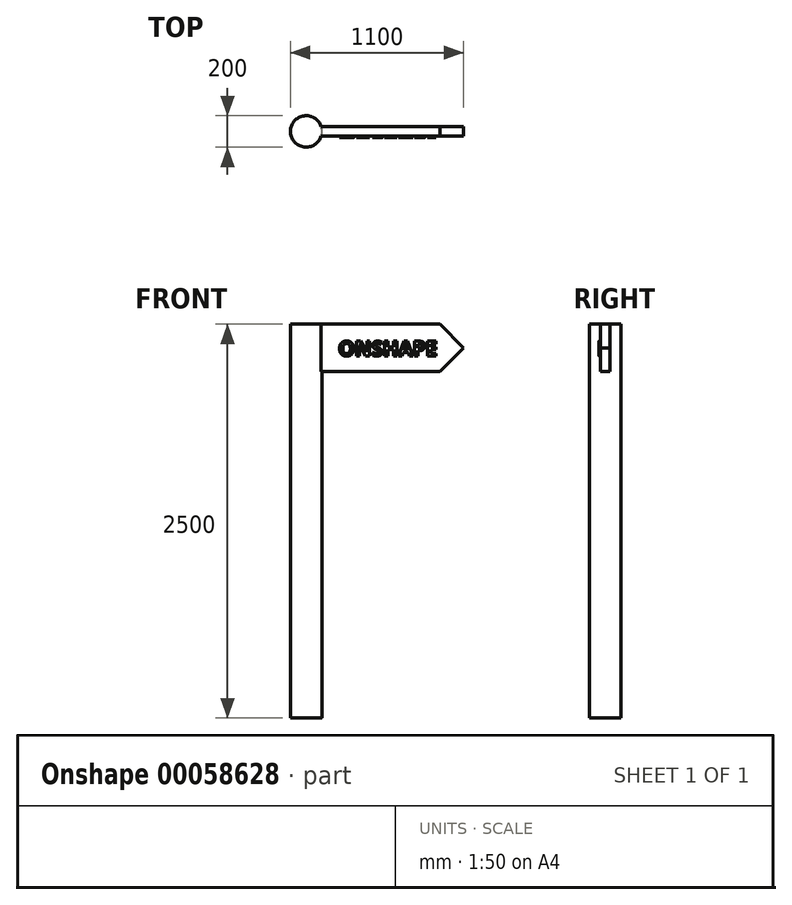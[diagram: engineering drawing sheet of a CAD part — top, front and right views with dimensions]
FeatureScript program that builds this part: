
annotation { "Feature Type Name" : "Feature", "Feature Type Description" : "" }
export const myFeature = defineFeature(function(context is Context, id is Id, definition is map)
    precondition{}
    {
        {
            var Q0;
            Q0=qCreatedBy(makeId("Top.planeOp"),FACE);
            var sketch = newSketch(context, id + "F0", { "sketchPlane" : qUnion([Q0])});
            skCircle(sketch, "E0", {"center": v(0, 0) * mm, "radius": 100 * mm});
            skSolve(sketch);
        }
        {
            var Q0;
            Q0 = qSketchRegion(id + "F0", true);
            extrude(context, id + "F1", {"entities" : qUnion([Q0]), "depth" : 2500 * mm});
        }
        {
            var Q0;
            Q0=qCreatedBy(makeId("Front.planeOp"),FACE);
            var sketch = newSketch(context, id + "F2", { "sketchPlane" : qUnion([Q0])});
            skLineSegment(sketch, "E1.bottom", {"start": v(0, 2500) * mm, "end": v(1000, 2500) * mm});
            skLineSegment(sketch, "E1.top", {"start": v(0, 2200) * mm, "end": v(1000, 2200) * mm});
            skLineSegment(sketch, "E1.left", {"start": v(0, 2500) * mm, "end": v(0, 2200) * mm});
            skLineSegment(sketch, "E1.right", {"start": v(1000, 2500) * mm, "end": v(1000, 2200) * mm});
            skLineSegment(sketch, "E2", {"start": v(1000, 2350) * mm, "end": v(850, 2500) * mm});
            skLineSegment(sketch, "E3", {"start": v(1000, 2350) * mm, "end": v(850, 2200) * mm});
            skSolve(sketch);
        }
        {
            var Q0;
            {var subQ1=sQuery(id+"F2.wireOp",EDGE,"E1.left");Q0=makeQuery(id+"F2.imprint","IMPRINT",FACE,{"disambiguationData":[TD([[makeQuery(id+"F2.imprint","IMPRINT",EDGE,{"derivedFrom":subQ1}),1.0]])]});}
            extrude(context, id + "F3", {"entities" : qUnion([Q0]), "operationType" : NewBodyOperationType.ADD, "endBound" : BoundingType.SYMMETRIC, "depth" : 60 * mm});
        }
        {
            var Q0;
            Q0=makeQuery(id+"F3.opExtrude","CAP_FACE",FACE,{"disambiguationData":[OSD([sQuery(id+"F2.wireOp",EDGE,"E1.bottom"),sQuery(id+"F2.wireOp",EDGE,"E1.top"),sQuery(id+"F2.wireOp",EDGE,"E1.left"),sQuery(id+"F2.wireOp",EDGE,"E2"),sQuery(id+"F2.wireOp",EDGE,"E3")])],"isStart":false});
            var sketch = newSketch(context, id + "F4", { "sketchPlane" : qUnion([Q0])});
            skText(sketch, "E4", { "text": "ONSHAPE", "fontName": "OpenSans-Bold.ttf"});
            skPoint(sketch, "E4.firstSnap0", {"position": v(95.4, 2298.81) * mm});
            const initialGuessF4  = {"E4": [0.20421, 2.29881, 1, 0, 0.09426]};
            skSetInitialGuess(sketch, initialGuessF4);
            skSolve(sketch);
        }
        {
            var Q0;
            Q0 = qSketchRegion(id + "F4", true);
            extrude(context, id + "F5", {"entities" : qUnion([Q0]), "operationType" : NewBodyOperationType.ADD, "depth" : 10 * mm});
        }
    });
